# Revit family: 6NDMLH-NRG
name_source: partatom
category: Mechanical Equipment
units: mm (PartAtom-declared; Revit-internal decimal feet)

## family parameters
Always vertical = Yes
Cut with Voids When Loaded = No
OmniClass Number = 23.40.40.11.17
OmniClass Title = Refrigerated Cases
Part Type = Normal
Room Calculation Point = No
Round Connector Dimension = Use Radius
Shared = No
Work Plane-Based = Yes

## types (8) — shared parameters
20" Shelf = Yes
BOTTOM ELECTRICAL = Yes
BOTTOM REFRIGERATION PIPING = Yes
Certifications = NSF 7, UL471, CSA
DATE = 03/13/2017
DESIGNERS NAME = SHIDDRAMESH
DRAIN PIPING = Yes
Default Elevation = 48"
Description = Narrow Multi-Deck Merchandiser with Synerg-E™
Discharge Air Velocity (FPM) = 260 FPM
EQUIPMENT DESCRIPTION = Narrow Multi-Deck Merchandiser with Synerg-E™
EQUIPMENT MARK = 6NDMLH-NRG
GLASS = Glass
Height = 88 5/8"
Item Description = Narrow Multi-Deck Merchandiser with Synerg-E™
LF STD END = Yes
Legend Number = 6NDMLH-NRG
Manufacturer = HILL PHOENIX
Model = 6NDMLH-NRG
PAINTED METAL UPPER SHELF = PAINTED SHELVES
REAR REFRIGERATION PIPING = Yes
REFRIGERATION PIPING = COPPER PIPE
RT STD END = Yes
SQUARE LH END = Yes
SQUARE RH END = Yes
STAINLESS STEEL = GALVANIZED STEEL
Standard Power Amps = 0 A
Superheat Set Point @ Bulb (°F) = 6-8 °F
TOP ELECTRICAL = Yes
TOP REFRIGERATION PIPING = Yes
Timed-Off Defrost Termination Temp = 42 °F
URL = http://www.hillphoenix.com
Width = 37 3/4"

## per-type parameters (varying)
- 04'(Dairy,Deli,Cut Produce): BTUH Conventional=1862; BTUH Parallel=1748; CENTER LINE=24"; DRAIN LINE=36"; Defrosts Per Day=6; Discharge Air (°F)=31 °F; Evaporator (°F)=28 °F; FULL VIEW LH END=Yes; FULL VIEW RH END=Yes; High Efficiency Amps=0 A; High Efficiency Watts=43 W; High Power (Cornice) Amps=0 A; High Power (Cornice) Watts=15 W; Length=48"; Length of Cases=48"; Light Length=4'; Lights Per Row=1; Number of Fans=2; REDUCED VIEW LH END=Yes; REDUCED VIEW RH END=Yes; Refgn=7 5/8"; SOLID EXT LH END=Yes; SOLID EXT RH END=Yes; SOLID STD LH END=Yes; SOLID STD RH END=Yes; SUPER VIEW LH END=Yes; SUPER VIEW RH END=Yes; Standard Power Watts=6 W; Timed-Off Defrost Fail-Safe (Min)=45
- 08'(Dairy,Deli,Cut Produce): BTUH Conventional=1862; BTUH Parallel=1748; CENTER LINE=48"; DRAIN LINE=48"; Defrosts Per Day=6; Discharge Air (°F)=31 °F; Evaporator (°F)=28 °F; FULL VIEW LH END=Yes; FULL VIEW RH END=Yes; High Efficiency Amps=1 A; High Efficiency Watts=65 W; High Power (Cornice) Amps=0 A; High Power (Cornice) Watts=30 W; Length=96"; Length of Cases=96"; Light Length=4'; Lights Per Row=2; Number of Fans=3; REDUCED VIEW LH END=Yes; REDUCED VIEW RH END=Yes; Refgn=8 3/4"; SOLID EXT LH END=Yes; SOLID EXT RH END=Yes; SOLID STD LH END=Yes; SOLID STD RH END=Yes; SUPER VIEW LH END=Yes; SUPER VIEW RH END=Yes; Standard Power Watts=12 W; Timed-Off Defrost Fail-Safe (Min)=45 (Min)
- 12'(Dairy,Deli,Cut Produce): BTUH Conventional=1862; BTUH Parallel=1748; CENTER LINE=72"; DRAIN LINE=72"; Defrosts Per Day=6; Discharge Air (°F)=31 °F; Evaporator (°F)=28 °F; FULL VIEW LH END=Yes; FULL VIEW RH END=Yes; High Efficiency Amps=1 A; High Efficiency Watts=87 W; High Power (Cornice) Amps=1 A; High Power (Cornice) Watts=65 W; Length=144"; Length of Cases=144"; Light Length=4'; Lights Per Row=3; Number of Fans=4; REDUCED VIEW LH END=Yes; REDUCED VIEW RH END=Yes; Refgn=8 3/4"; SOLID EXT LH END=Yes; SOLID EXT RH END=Yes; SOLID STD LH END=Yes; SOLID STD RH END=Yes; SUPER VIEW LH END=Yes; SUPER VIEW RH END=Yes; Standard Power Watts=36 W; Timed-Off Defrost Fail-Safe (Min)=45 (Min)
- 06'(Dairy,Deli,Cut Produce): BTUH Conventional=1860; BTUH Parallel=1819; CENTER LINE=36"; DRAIN LINE=48"; Defrosts Per Day=2; Discharge Air (°F)=37 °F; Evaporator (°F)=34 °F; FULL VIEW LH END=Yes; FULL VIEW RH END=Yes; High Efficiency Amps=1 A; High Efficiency Watts=65 W; High Power (Cornice) Amps=0 A; High Power (Cornice) Watts=24 W; Length=72"; Length of Cases=72"; Light Length=3'; Lights Per Row=2; Number of Fans=3; REDUCED VIEW LH END=Yes; REDUCED VIEW RH END=Yes; Refgn=8 3/4"; SOLID EXT LH END=Yes; SOLID EXT RH END=Yes; SOLID STD LH END=Yes; SOLID STD RH END=Yes; SUPER VIEW LH END=Yes; SUPER VIEW RH END=Yes; Standard Power Watts=9 W; Timed-Off Defrost Fail-Safe (Min)=30
- 04'(Bulk Produce,Beverage): BTUH Conventional=1860; BTUH Parallel=1819; CENTER LINE=24"; DRAIN LINE=36"; Defrosts Per Day=2; Discharge Air (°F)=37 °F; Evaporator (°F)=34 °F; FULL VIEW LH END=Yes; FULL VIEW RH END=Yes; High Efficiency Amps=0 A; High Efficiency Watts=43 W; High Power (Cornice) Amps=0 A; High Power (Cornice) Watts=22 W; Length=48"; Length of Cases=48"; Light Length=4'; Lights Per Row=1; Number of Fans=2; REDUCED VIEW LH END=Yes; REDUCED VIEW RH END=Yes; Refgn=7 5/8"; SOLID EXT LH END=Yes; SOLID EXT RH END=Yes; SOLID STD LH END=Yes; SOLID STD RH END=Yes; SUPER VIEW LH END=Yes; SUPER VIEW RH END=Yes; Standard Power Watts=12 W; Timed-Off Defrost Fail-Safe (Min)="30 (Min)"
- 06'(Bulk Produce,Beverage): BTUH Conventional=1860; BTUH Parallel=1819; CENTER LINE=36"; DRAIN LINE=48"; Defrosts Per Day=2; Discharge Air (°F)=37 °F; Evaporator (°F)=34 °F; FULL VIEW LH END=Yes; FULL VIEW RH END=Yes; High Efficiency Amps=1 A; High Efficiency Watts=65 W; High Power (Cornice) Amps=0 A; High Power (Cornice) Watts=30 W; Length=72"; Length of Cases=72"; Light Length=3'; Lights Per Row=2; Number of Fans=3; REDUCED VIEW LH END=Yes; REDUCED VIEW RH END=Yes; Refgn=8 3/4"; SOLID EXT LH END=Yes; SOLID EXT RH END=Yes; SOLID STD LH END=Yes; SOLID STD RH END=Yes; SUPER VIEW LH END=Yes; SUPER VIEW RH END=Yes; Standard Power Watts=17 W; Timed-Off Defrost Fail-Safe (Min)="30 (Min) "
- 08'(Bulk Produce,Beverage): BTUH Conventional=1860; BTUH Parallel=1819; CENTER LINE=48"; DRAIN LINE=48"; Defrosts Per Day=2; Discharge Air (°F)=37 °F; Evaporator (°F)=34 °F; FULL VIEW LH END=Yes; FULL VIEW RH END=Yes; High Efficiency Amps=1 A; High Efficiency Watts=65 W; High Power (Cornice) Amps=0 A; High Power (Cornice) Watts=43 W; Length=96"; Length of Cases=96"; Light Length=4'; Lights Per Row=2; Number of Fans=3; REDUCED VIEW LH END=Yes; REDUCED VIEW RH END=Yes; Refgn=8 3/4"; SOLID EXT LH END=Yes; SOLID EXT RH END=Yes; SOLID STD LH END=Yes; SOLID STD RH END=Yes; SUPER VIEW LH END=Yes; SUPER VIEW RH END=Yes; Standard Power Watts=24 W; Timed-Off Defrost Fail-Safe (Min)="30 (Min) "
- 12'(Bulk Produce,Beverage): BTUH Conventional=1860; BTUH Parallel=1819; CENTER LINE=72"; DRAIN LINE=72"; Defrosts Per Day=2; Discharge Air (°F)=37 °F; Evaporator (°F)=34 °F; FULL VIEW LH END=No; FULL VIEW RH END=No; High Efficiency Amps=1 A; High Efficiency Watts=87 W; High Power (Cornice) Amps=1 A; High Power (Cornice) Watts=65 W; Length=144"; Length of Cases=144"; Light Length=4'; Lights Per Row=3; Number of Fans=4; REDUCED VIEW LH END=No; REDUCED VIEW RH END=No; Refgn=8 3/4"; SOLID EXT LH END=No; SOLID EXT RH END=No; SOLID STD LH END=No; SOLID STD RH END=No; SUPER VIEW LH END=No; SUPER VIEW RH END=No; Standard Power Watts=36 W; Timed-Off Defrost Fail-Safe (Min)="30 (Min) "

## geometry (parser evidence)
native form markers: Blend x19, Sweep x9
no freeform markers — native parametric forms only
